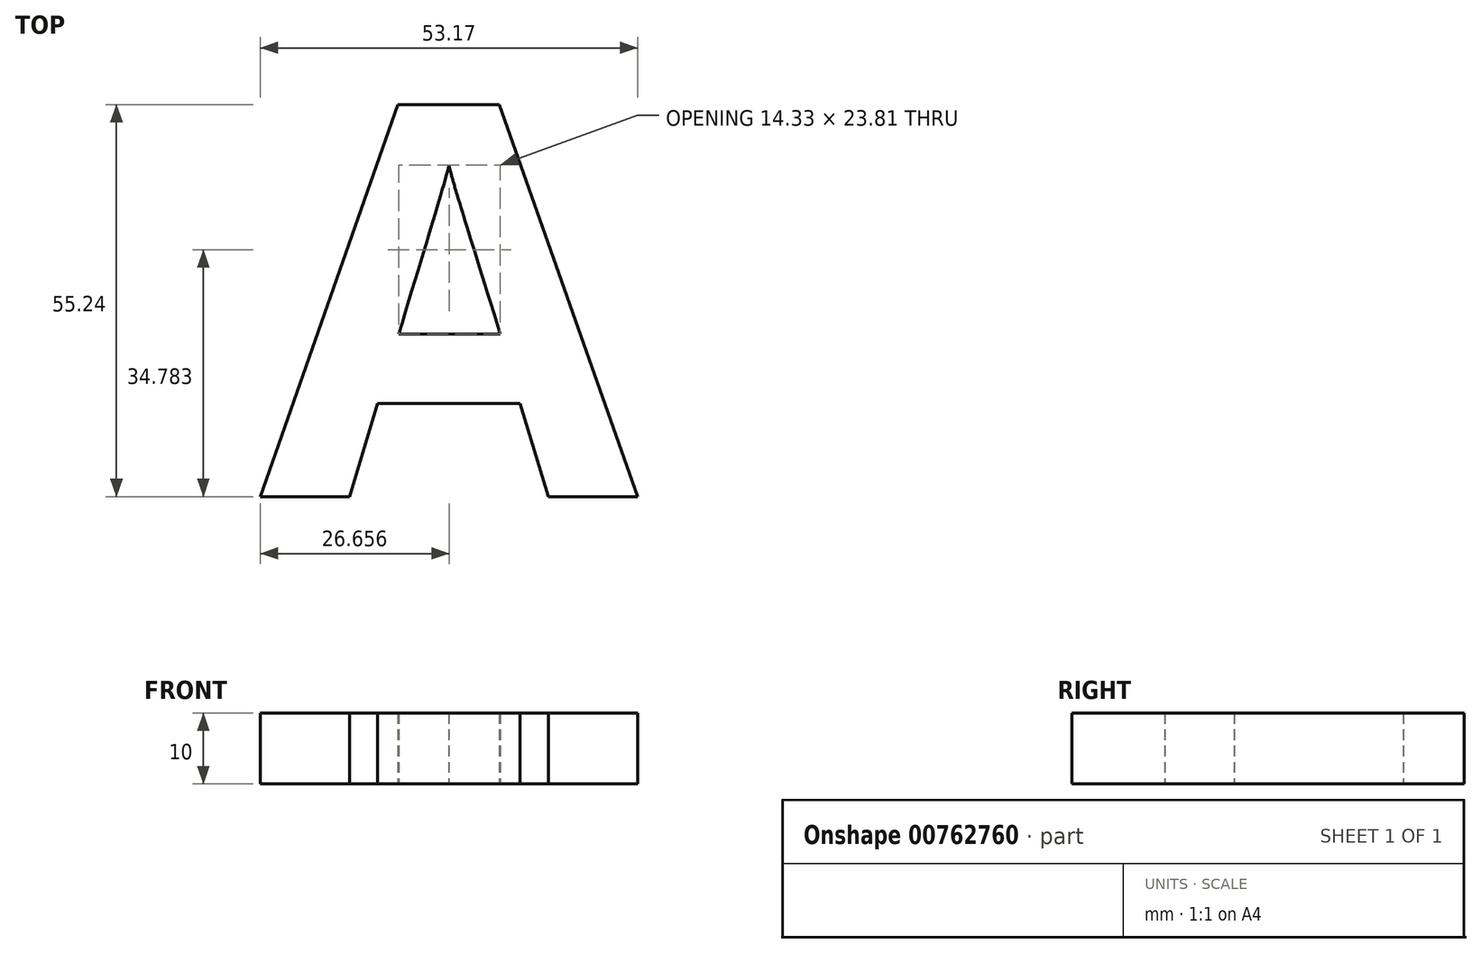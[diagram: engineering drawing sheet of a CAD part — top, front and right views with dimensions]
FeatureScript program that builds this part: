
annotation { "Feature Type Name" : "Feature", "Feature Type Description" : "" }
export const myFeature = defineFeature(function(context is Context, id is Id, definition is map)
    precondition{}
    {
        {
            var Q0;
            Q0=qCreatedBy(makeId("Top.planeOp"),FACE);
            var sketch = newSketch(context, id + "F0", { "sketchPlane" : qUnion([Q0])});
            skText(sketch, "E0", { "text": "A", "fontName": "OpenSans-Bold.ttf"});
            const initialGuessF0  = {"E0": [0, 0, 1, 0, 0.05548]};
            skSetInitialGuess(sketch, initialGuessF0);
            skSolve(sketch);
        }
        {
            var Q0;
            Q0 = qSketchRegion(id + "F0", true);
            extrude(context, id + "F1", {"entities" : qUnion([Q0]), "depth" : 10 * mm, "offsetDistance" : 25 * mm});
        }
    });
